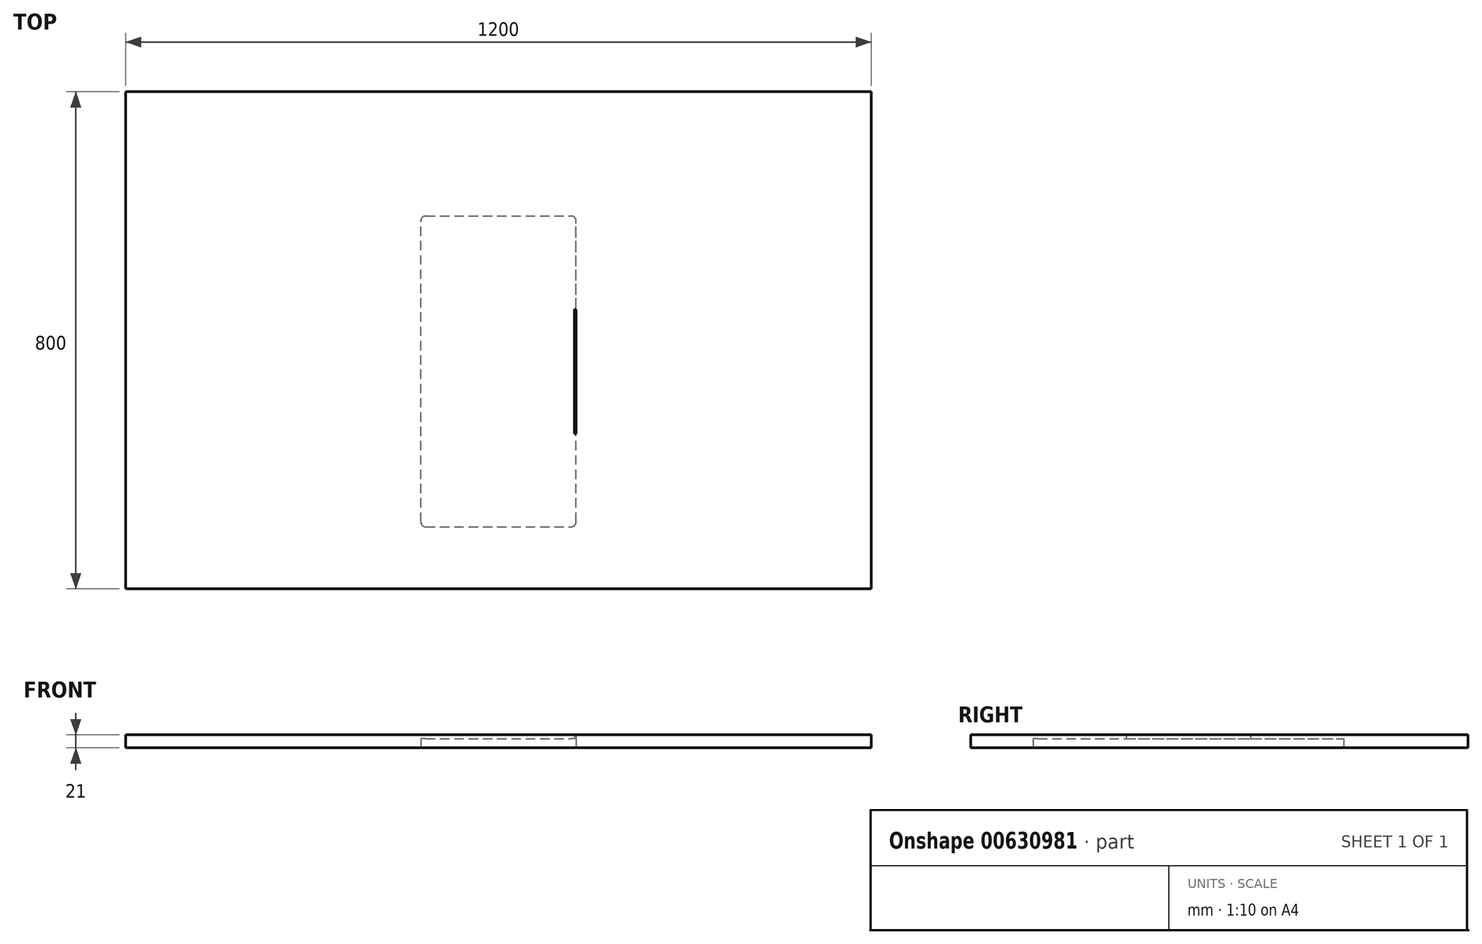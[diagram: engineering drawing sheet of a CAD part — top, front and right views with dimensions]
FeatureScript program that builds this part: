
annotation { "Feature Type Name" : "Feature", "Feature Type Description" : "" }
export const myFeature = defineFeature(function(context is Context, id is Id, definition is map)
    precondition{}
    {
        {
            var Q0;
            Q0=qCreatedBy(makeId("Top.planeOp"),FACE);
            var sketch = newSketch(context, id + "F0", { "sketchPlane" : qUnion([Q0])});
            skLineSegment(sketch, "E0.bottom", {"start": v(-600.65, 501.97) * mm, "end": v(599.35, 501.97) * mm});
            skLineSegment(sketch, "E0.top", {"start": v(-600.65, -298.03) * mm, "end": v(599.35, -298.03) * mm});
            skLineSegment(sketch, "E0.left", {"start": v(-600.65, 501.97) * mm, "end": v(-600.65, -298.03) * mm});
            skLineSegment(sketch, "E0.right", {"start": v(599.35, 501.97) * mm, "end": v(599.35, -298.03) * mm});
            skSolve(sketch);
        }
        {
            var Q0;
            Q0=makeQuery(id+"F0.imprint","IMPRINT",FACE,{"disambiguationData":[TD([[makeQuery(id+"F0.imprint","IMPRINT",EDGE,{"derivedFrom":sQuery(id+"F0.wireOp",EDGE,"E0.bottom")}),-1.0]])]});
            extrude(context, id + "F1", {"entities" : qUnion([Q0]), "depth" : 21 * mm, "offsetDistance" : 25 * mm});
        }
        {
            var Q0;
            Q0=makeQuery(id+"F1.opExtrude","CAP_FACE",FACE,{"disambiguationData":[OSD([sQuery(id+"F0.wireOp",EDGE,"E0.bottom"),sQuery(id+"F0.wireOp",EDGE,"E0.top"),sQuery(id+"F0.wireOp",EDGE,"E0.left"),sQuery(id+"F0.wireOp",EDGE,"E0.right")])],"isStart":true});
            var sketch = newSketch(context, id + "F2", { "sketchPlane" : qUnion([Q0])});
            skLineSegment(sketch, "E1.bottom", {"start": v(-125.65, 198.03) * mm, "end": v(124.35, 198.03) * mm});
            skLineSegment(sketch, "E1.top", {"start": v(-125.65, -301.97) * mm, "end": v(124.35, -301.97) * mm});
            skLineSegment(sketch, "E1.left", {"start": v(-125.65, 198.03) * mm, "end": v(-125.65, -301.97) * mm});
            skLineSegment(sketch, "E1.right", {"start": v(124.35, 198.03) * mm, "end": v(124.35, -301.97) * mm});
            skSolve(sketch);
        }
        {
            var Q0;
            Q0 = qSketchRegion(id + "F2", true);
            extrude(context, id + "F3", {"entities" : qUnion([Q0]), "operationType" : NewBodyOperationType.REMOVE, "oppositeDirection" : true, "depth" : 15 * mm, "offsetDistance" : 25 * mm});
        }
        {
            var Q0;
            Q0=makeQuery(id+"F3.boolean.opBoolean","COPY",EDGE,{"derivedFrom":makeQuery(id+"F3.opExtrude","SWEPT_EDGE",EDGE,{"disambiguationData":[OSD([sQuery(id+"F2.wireOp",EDGE,"E1.bottom"),sQuery(id+"F2.wireOp",EDGE,"E1.left")])]})});
            fillet(context, id + "F4", {"entities" : qUnion([Q0]), "radius" : 8 * mm, "tangentPropagation" : true, "allowEdgeOverflow" : false});
        }
        {
            var Q0;
            Q0=makeQuery(id+"F3.boolean.opBoolean","COPY",EDGE,{"derivedFrom":makeQuery(id+"F3.opExtrude","SWEPT_EDGE",EDGE,{"disambiguationData":[OSD([sQuery(id+"F2.wireOp",EDGE,"E1.top"),sQuery(id+"F2.wireOp",EDGE,"E1.right")])]})});
            fillet(context, id + "F5", {"entities" : qUnion([Q0]), "radius" : 8 * mm, "tangentPropagation" : true, "allowEdgeOverflow" : false});
        }
        {
            var Q0;
            Q0=makeQuery(id+"F3.boolean.opBoolean","COPY",EDGE,{"derivedFrom":makeQuery(id+"F3.opExtrude","SWEPT_EDGE",EDGE,{"disambiguationData":[OSD([sQuery(id+"F2.wireOp",EDGE,"E1.bottom"),sQuery(id+"F2.wireOp",EDGE,"E1.right")])]})});
            fillet(context, id + "F6", {"entities" : qUnion([Q0]), "radius" : 8 * mm, "tangentPropagation" : true, "allowEdgeOverflow" : false});
        }
        {
            var Q0;
            Q0=makeQuery(id+"F3.boolean.opBoolean","COPY",EDGE,{"derivedFrom":makeQuery(id+"F3.opExtrude","SWEPT_EDGE",EDGE,{"disambiguationData":[OSD([sQuery(id+"F2.wireOp",EDGE,"E1.top"),sQuery(id+"F2.wireOp",EDGE,"E1.left")])]})});
            fillet(context, id + "F7", {"entities" : qUnion([Q0]), "radius" : 8 * mm, "tangentPropagation" : true, "allowEdgeOverflow" : false});
        }
        {
            var Q0;
            Q0=makeQuery(id+"F3.boolean.opBoolean","COPY",FACE,{"derivedFrom":makeQuery(id+"F3.opExtrude","CAP_FACE",FACE,{"disambiguationData":[OSD([sQuery(id+"F2.wireOp",EDGE,"E1.bottom"),sQuery(id+"F2.wireOp",EDGE,"E1.top"),sQuery(id+"F2.wireOp",EDGE,"E1.left"),sQuery(id+"F2.wireOp",EDGE,"E1.right")])],"isStart":false})});
            var sketch = newSketch(context, id + "F8", { "sketchPlane" : qUnion([Q0])});
            skLineSegment(sketch, "E2.bottom", {"start": v(124.35, 48.03) * mm, "end": v(121.35, 48.03) * mm});
            skLineSegment(sketch, "E2.top", {"start": v(124.35, -151.97) * mm, "end": v(121.35, -151.97) * mm});
            skLineSegment(sketch, "E2.left", {"start": v(124.35, 48.03) * mm, "end": v(124.35, -151.97) * mm});
            skLineSegment(sketch, "E2.right", {"start": v(121.35, 48.03) * mm, "end": v(121.35, -151.97) * mm});
            skSolve(sketch);
        }
        {
            var Q0;
            Q0 = qSketchRegion(id + "F8", true);
            extrude(context, id + "F9", {"entities" : qUnion([Q0]), "operationType" : NewBodyOperationType.REMOVE, "oppositeDirection" : true, "depth" : 25 * mm, "offsetDistance" : 25 * mm});
        }
    });
